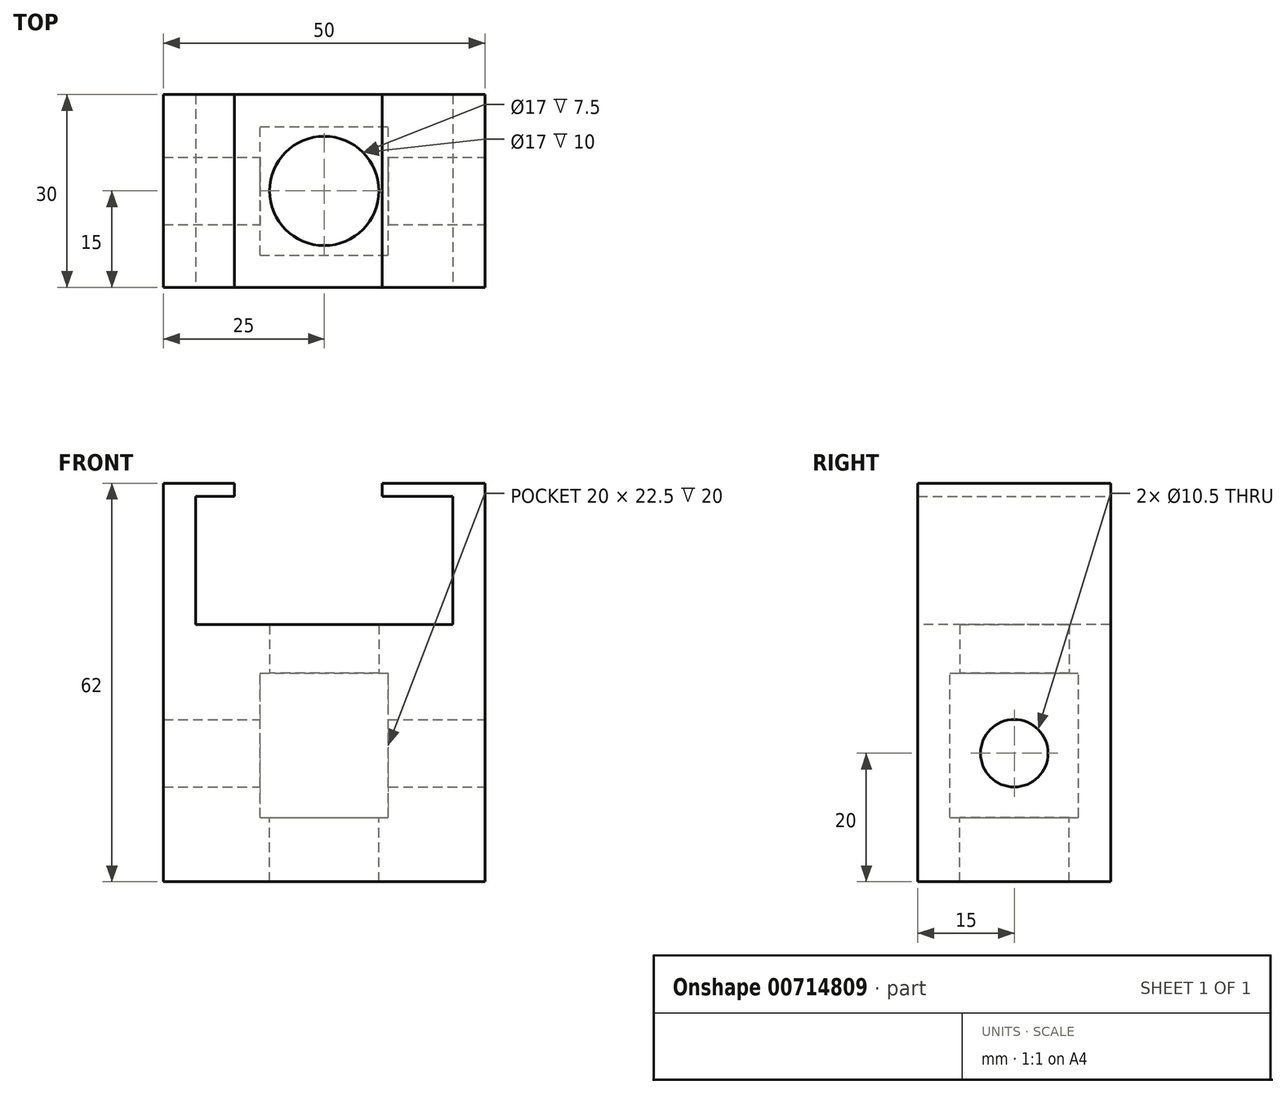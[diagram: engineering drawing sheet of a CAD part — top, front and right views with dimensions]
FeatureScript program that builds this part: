
annotation { "Feature Type Name" : "Feature", "Feature Type Description" : "" }
export const myFeature = defineFeature(function(context is Context, id is Id, definition is map)
    precondition{}
    {
        {
            var Q0;
            Q0=qCreatedBy(makeId("Top.planeOp"),FACE);
            var sketch = newSketch(context, id + "F0", { "sketchPlane" : qUnion([Q0])});
            skCircle(sketch, "E0", {"center": v(0, 0) * mm, "radius": 8.5 * mm});
            skSolve(sketch);
        }
        {
            var Q0;
            Q0=qCreatedBy(makeId("Top.planeOp"),FACE);
            cPlane(context, id + "F1", {"entities" : qUnion([Q0]), "cplaneType" : CPlaneType.OFFSET, "offset" : 20 * mm, "width" : 150 * mm, "height" : 150 * mm});
        }
        {
            var Q0;
            Q0=qCreatedBy(id+"F1.planeOp",FACE);
            var sketch = newSketch(context, id + "F2", { "sketchPlane" : qUnion([Q0])});
            skLineSegment(sketch, "E1.bottom", {"start": v(-25, 15) * mm, "end": v(25, 15) * mm});
            skLineSegment(sketch, "E1.top", {"start": v(-25, -15) * mm, "end": v(25, -15) * mm});
            skLineSegment(sketch, "E1.left", {"start": v(-25, 15) * mm, "end": v(-25, -15) * mm});
            skLineSegment(sketch, "E1.right", {"start": v(25, 15) * mm, "end": v(25, -15) * mm});
            skPoint(sketch, "E1.middle", {"position": v(0, 0) * mm});
            skSolve(sketch);
        }
        {
            var Q0;
            Q0=makeQuery(id+"F2.imprint","IMPRINT",FACE,{"disambiguationData":[TD([[makeQuery(id+"F2.imprint","IMPRINT",EDGE,{"derivedFrom":sQuery(id+"F2.wireOp",EDGE,"E1.bottom")}),-1.0]])]});
            extrude(context, id + "F3", {"entities" : qUnion([Q0]), "oppositeDirection" : true, "depth" : 30 * mm, "offsetDistance" : 25 * mm});
        }
        {
            var Q0;
            Q0 = qSketchRegion(id + "F0", true);
            extrude(context, id + "F4", {"entities" : qUnion([Q0]), "operationType" : NewBodyOperationType.REMOVE, "depth" : 20 * mm, "offsetDistance" : 25 * mm});
        }
        {
            var Q0;
            Q0=makeQuery(id+"F3.opExtrude","CAP_FACE",FACE,{"disambiguationData":[OSD([sQuery(id+"F2.wireOp",EDGE,"E1.bottom"),sQuery(id+"F2.wireOp",EDGE,"E1.top"),sQuery(id+"F2.wireOp",EDGE,"E1.left"),sQuery(id+"F2.wireOp",EDGE,"E1.right")])],"isStart":true});
            var sketch = newSketch(context, id + "F5", { "sketchPlane" : qUnion([Q0])});
            skLineSegment(sketch, "E2.bottom", {"start": v(-25, 15) * mm, "end": v(-20, 15) * mm});
            skLineSegment(sketch, "E2.top", {"start": v(-25, -15) * mm, "end": v(-20, -15) * mm});
            skLineSegment(sketch, "E2.left", {"start": v(-25, 15) * mm, "end": v(-25, -15) * mm});
            skLineSegment(sketch, "E2.right", {"start": v(-20, 15) * mm, "end": v(-20, -15) * mm});
            skLineSegment(sketch, "E3.bottom", {"start": v(25, 15) * mm, "end": v(20, 15) * mm});
            skLineSegment(sketch, "E3.top", {"start": v(25, -15) * mm, "end": v(20, -15) * mm});
            skLineSegment(sketch, "E3.left", {"start": v(25, 15) * mm, "end": v(25, -15) * mm});
            skLineSegment(sketch, "E3.right", {"start": v(20, 15) * mm, "end": v(20, -15) * mm});
            skSolve(sketch);
        }
        {
            var Q0;
            Q0 = qSketchRegion(id + "F5", true);
            extrude(context, id + "F6", {"entities" : qUnion([Q0]), "operationType" : NewBodyOperationType.ADD, "depth" : 22 * mm, "offsetDistance" : 25 * mm});
        }
        {
            var Q0;
            Q0=makeQuery(id+"F6.opExtrude","SWEPT_FACE",FACE,{"disambiguationData":[OSD([sQuery(id+"F5.wireOp",EDGE,"E2.right")])]});
            var sketch = newSketch(context, id + "F7", { "sketchPlane" : qUnion([Q0])});
            skLineSegment(sketch, "E4.bottom", {"start": v(-15, 42) * mm, "end": v(15, 42) * mm});
            skLineSegment(sketch, "E4.top", {"start": v(-15, 40) * mm, "end": v(15, 40) * mm});
            skLineSegment(sketch, "E4.left", {"start": v(-15, 42) * mm, "end": v(-15, 40) * mm});
            skLineSegment(sketch, "E4.right", {"start": v(15, 42) * mm, "end": v(15, 40) * mm});
            skSolve(sketch);
        }
        {
            var Q0;
            Q0 = qSketchRegion(id + "F7", true);
            extrude(context, id + "F8", {"entities" : qUnion([Q0]), "operationType" : NewBodyOperationType.ADD, "depth" : 6 * mm, "offsetDistance" : 25 * mm});
        }
        {
            var Q0;
            Q0=makeQuery(id+"F6.opExtrude","SWEPT_FACE",FACE,{"disambiguationData":[OSD([sQuery(id+"F5.wireOp",EDGE,"E3.right")])]});
            var sketch = newSketch(context, id + "F9", { "sketchPlane" : qUnion([Q0])});
            skLineSegment(sketch, "E5.bottom", {"start": v(15, 42) * mm, "end": v(-15, 42) * mm});
            skLineSegment(sketch, "E5.top", {"start": v(15, 40) * mm, "end": v(-15, 40) * mm});
            skLineSegment(sketch, "E5.left", {"start": v(15, 42) * mm, "end": v(15, 40) * mm});
            skLineSegment(sketch, "E5.right", {"start": v(-15, 42) * mm, "end": v(-15, 40) * mm});
            skSolve(sketch);
        }
        {
            var Q0;
            Q0 = qSketchRegion(id + "F9", true);
            extrude(context, id + "F10", {"entities" : qUnion([Q0]), "operationType" : NewBodyOperationType.ADD, "depth" : 11 * mm, "offsetDistance" : 25 * mm});
        }
        {
            var Q0;
            Q0=qCreatedBy(makeId("Top.planeOp"),FACE);
            var sketch = newSketch(context, id + "F11", { "sketchPlane" : qUnion([Q0])});
            skLineSegment(sketch, "E6.bottom", {"start": v(-10, -10) * mm, "end": v(10, -10) * mm});
            skLineSegment(sketch, "E6.top", {"start": v(-10, 10) * mm, "end": v(10, 10) * mm});
            skLineSegment(sketch, "E6.left", {"start": v(-10, -10) * mm, "end": v(-10, 10) * mm});
            skLineSegment(sketch, "E6.right", {"start": v(10, -10) * mm, "end": v(10, 10) * mm});
            skPoint(sketch, "E6.middle", {"position": v(0, 0) * mm});
            skSolve(sketch);
        }
        {
            var Q0;
            Q0 = qSketchRegion(id + "F11", true);
            extrude(context, id + "F12", {"entities" : qUnion([Q0]), "operationType" : NewBodyOperationType.REMOVE, "endBound" : BoundingType.SYMMETRIC, "oppositeDirection" : true, "depth" : 25 * mm, "offsetDistance" : 25 * mm});
        }
        {
            var Q0;
            Q0=makeQuery(id+"F3.opExtrude","CAP_FACE",FACE,{"disambiguationData":[OSD([sQuery(id+"F2.wireOp",EDGE,"E1.bottom"),sQuery(id+"F2.wireOp",EDGE,"E1.top"),sQuery(id+"F2.wireOp",EDGE,"E1.left"),sQuery(id+"F2.wireOp",EDGE,"E1.right")])],"isStart":false});
            var sketch = newSketch(context, id + "F13", { "sketchPlane" : qUnion([Q0])});
            skLineSegment(sketch, "E7.bottom", {"start": v(-25, -15) * mm, "end": v(25, -15) * mm});
            skLineSegment(sketch, "E7.top", {"start": v(-25, 15) * mm, "end": v(25, 15) * mm});
            skLineSegment(sketch, "E7.left", {"start": v(-25, -15) * mm, "end": v(-25, 15) * mm});
            skLineSegment(sketch, "E7.right", {"start": v(25, -15) * mm, "end": v(25, 15) * mm});
            skSolve(sketch);
        }
        {
            var Q0;
            Q0 = qSketchRegion(id + "F13", true);
            extrude(context, id + "F14", {"entities" : qUnion([Q0]), "operationType" : NewBodyOperationType.ADD, "depth" : 10 * mm, "offsetDistance" : 25 * mm});
        }
        {
            var Q0;
            Q0 = qSketchRegion(id + "F0", true);
            extrude(context, id + "F15", {"entities" : qUnion([Q0]), "operationType" : NewBodyOperationType.REMOVE, "oppositeDirection" : true, "depth" : 25 * mm, "offsetDistance" : 25 * mm});
        }
        {
            var Q0;
            Q0=makeQuery(id+"F14.boolean.opBoolean","MERGE",FACE,{"derivedFrom":[makeQuery(id+"FhQ1VPa6iNNspAz_1.boolean.opBoolean","MERGE",FACE,{"derivedFrom":[makeQuery(id+"F6.boolean.opBoolean","MERGE",FACE,{"derivedFrom":[makeQuery(id+"F3.opExtrude","SWEPT_FACE",FACE,{"disambiguationData":[OSD([sQuery(id+"F2.wireOp",EDGE,"E1.right")])]}),makeQuery(id+"F6.opExtrude","SWEPT_FACE",FACE,{"disambiguationData":[OSD([sQuery(id+"F5.wireOp",EDGE,"E3.left")])]})]}),makeQuery(id+"FhQ1VPa6iNNspAz_1.opExtrude","SWEPT_FACE",FACE,{"disambiguationData":[OSD([sQuery(id+"F1EktrSovRmU546_1.wireOp",EDGE,"SWoF9eqy-vYb0-rAhZ-Gfrm-oLrZiuGwknWY.left")])]})]}),makeQuery(id+"F14.opExtrude","SWEPT_FACE",FACE,{"disambiguationData":[OSD([sQuery(id+"F13.wireOp",EDGE,"E7.right")])]})]});
            var sketch = newSketch(context, id + "F16", { "sketchPlane" : qUnion([Q0])});
            skCircle(sketch, "E8", {"center": v(0, 0) * mm, "radius": 5.25 * mm});
            skSolve(sketch);
        }
        {
            var Q0;
            Q0 = qSketchRegion(id + "F16", true);
            extrude(context, id + "F17", {"entities" : qUnion([Q0]), "operationType" : NewBodyOperationType.REMOVE, "oppositeDirection" : true, "depth" : 50 * mm, "offsetDistance" : 25 * mm});
        }
    });
